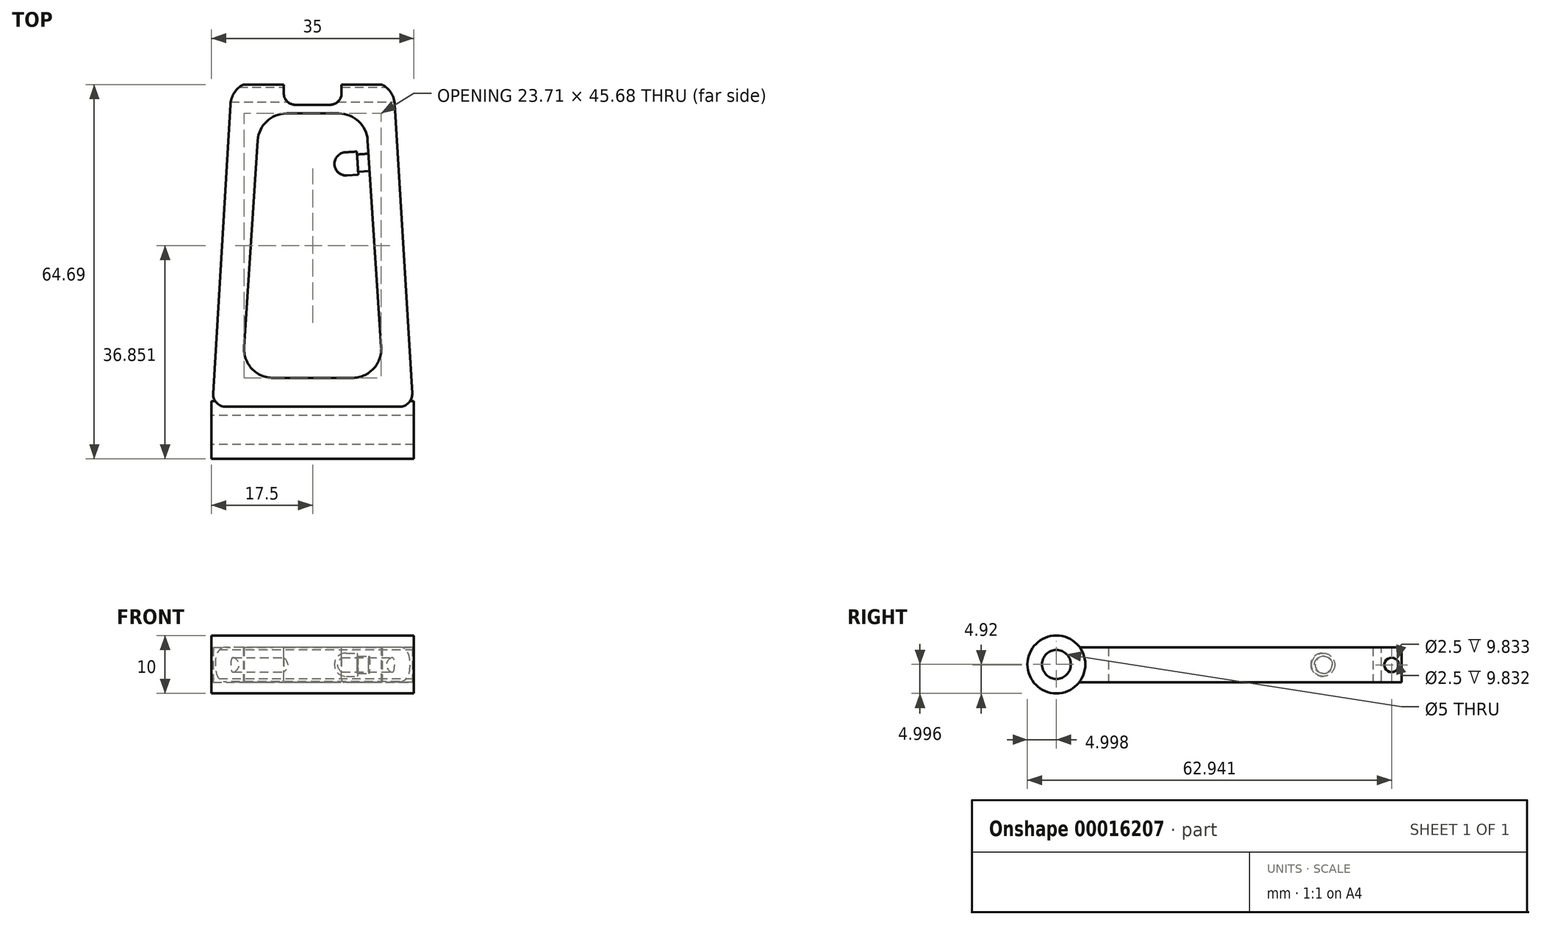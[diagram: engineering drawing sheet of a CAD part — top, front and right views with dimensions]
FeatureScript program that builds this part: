
annotation { "Feature Type Name" : "Feature", "Feature Type Description" : "" }
export const myFeature = defineFeature(function(context is Context, id is Id, definition is map)
    precondition{}
    {
        {
            var Q0;
            Q0=qCreatedBy(makeId("Top.planeOp"),FACE);
            var sketch = newSketch(context, id + "F0", { "sketchPlane" : qUnion([Q0])});
            skLineSegment(sketch, "E0", {"start": v(0, 0) * mm, "end": v(-15, 0) * mm});
            skArc(sketch, "E1", {"start": v(-15, 0) * mm, "mid": v(-16.6, 0.7) * mm, "end": v(-17.2, 2.34) * mm});
            skLineSegment(sketch, "E2", {"start": v(-17.2, 2.34) * mm, "end": v(-14.2, 52.25) * mm});
            skLineSegment(sketch, "E3", {"start": v(0, 28.16) * mm, "end": v(0, 0) * mm, "construction": true});
            skLineSegment(sketch, "E4.MirrorCS", {"start": v(17.2, 2.34) * mm, "end": v(14.2, 52.25) * mm});
            skArc(sketch, "E5.MirrorCS", {"start": v(15, 0) * mm, "mid": v(16.6, 0.7) * mm, "end": v(17.2, 2.34) * mm});
            skLineSegment(sketch, "E6.MirrorCS", {"start": v(0, 0) * mm, "end": v(15, 0) * mm});
            skArc(sketch, "E7", {"start": v(-14.2, 52.25) * mm, "mid": v(-13.55, 54.25) * mm, "end": v(-12, 55.68) * mm});
            skLineSegment(sketch, "E8", {"start": v(-12, 55.68) * mm, "end": v(0, 55.68) * mm});
            skLineSegment(sketch, "E9.MirrorCS", {"start": v(12, 55.68) * mm, "end": v(0, 55.68) * mm});
            skArc(sketch, "E10.MirrorCS", {"start": v(14.2, 52.25) * mm, "mid": v(13.55, 54.25) * mm, "end": v(12, 55.68) * mm});
            skLineSegment(sketch, "E11", {"start": v(-9.2, 50.68) * mm, "end": v(-12.2, 5) * mm});
            skLineSegment(sketch, "E12", {"start": v(-9.2, 50.68) * mm, "end": v(0, 50.68) * mm});
            skLineSegment(sketch, "E13", {"start": v(-12.2, 5) * mm, "end": v(0, 5) * mm});
            skLineSegment(sketch, "E14.MirrorCS", {"start": v(9.2, 50.68) * mm, "end": v(0, 50.68) * mm});
            skLineSegment(sketch, "E15.MirrorCS", {"start": v(9.2, 50.68) * mm, "end": v(12.2, 5) * mm});
            skLineSegment(sketch, "E16.MirrorCS", {"start": v(12.2, 5) * mm, "end": v(0, 5) * mm});
            skSolve(sketch);
        }
        {
            var Q0;
            Q0=makeQuery(id+"F0.imprint","IMPRINT",FACE,{"disambiguationData":[TD([[makeQuery(id+"F0.imprint","IMPRINT",EDGE,{"derivedFrom":sQuery(id+"F0.wireOp",EDGE,"E0")}),-1.0]])]});
            extrude(context, id + "F1", {"entities" : qUnion([Q0]), "depth" : 6 * mm});
        }
        {
            var Q0;
            Q0=makeQuery(id+"F1.opExtrude","SWEPT_EDGE",EDGE,{"disambiguationData":[OSD([sQuery(id+"F0.wireOp",EDGE,"E14.MirrorCS"),sQuery(id+"F0.wireOp",EDGE,"E15.MirrorCS")])]});
            var Q1;
            Q1=makeQuery(id+"F1.opExtrude","SWEPT_EDGE",EDGE,{"disambiguationData":[OSD([sQuery(id+"F0.wireOp",EDGE,"E15.MirrorCS"),sQuery(id+"F0.wireOp",EDGE,"E16.MirrorCS")])]});
            var Q2;
            Q2=makeQuery(id+"F1.opExtrude","SWEPT_EDGE",EDGE,{"disambiguationData":[OSD([sQuery(id+"F0.wireOp",EDGE,"E11"),sQuery(id+"F0.wireOp",EDGE,"E13")])]});
            var Q3;
            Q3=makeQuery(id+"F1.opExtrude","SWEPT_EDGE",EDGE,{"disambiguationData":[OSD([sQuery(id+"F0.wireOp",EDGE,"E11"),sQuery(id+"F0.wireOp",EDGE,"E12")])]});
            fillet(context, id + "F2", {"entities" : qUnion([Q0, Q1, Q2, Q3]), "radius" : 5 * mm, "tangentPropagation" : true, "allowEdgeOverflow" : false});
        }
        {
            var Q0;
            Q0=makeQuery(id+"F1.opExtrude","CAP_FACE",FACE,{"disambiguationData":[OSD([sQuery(id+"F0.wireOp",EDGE,"E0"),sQuery(id+"F0.wireOp",EDGE,"E1"),sQuery(id+"F0.wireOp",EDGE,"E2"),sQuery(id+"F0.wireOp",EDGE,"E4.MirrorCS"),sQuery(id+"F0.wireOp",EDGE,"E5.MirrorCS"),sQuery(id+"F0.wireOp",EDGE,"E6.MirrorCS"),sQuery(id+"F0.wireOp",EDGE,"E7"),sQuery(id+"F0.wireOp",EDGE,"E8"),sQuery(id+"F0.wireOp",EDGE,"E9.MirrorCS"),sQuery(id+"F0.wireOp",EDGE,"E10.MirrorCS"),sQuery(id+"F0.wireOp",EDGE,"E11"),sQuery(id+"F0.wireOp",EDGE,"E12"),sQuery(id+"F0.wireOp",EDGE,"E13"),sQuery(id+"F0.wireOp",EDGE,"E14.MirrorCS"),sQuery(id+"F0.wireOp",EDGE,"E15.MirrorCS"),sQuery(id+"F0.wireOp",EDGE,"E16.MirrorCS")])],"isStart":false});
            var sketch = newSketch(context, id + "F3", { "sketchPlane" : qUnion([Q0])});
            skLineSegment(sketch, "E17.rect.bottom", {"start": v(5, 55.68) * mm, "end": v(-5, 55.68) * mm});
            skLineSegment(sketch, "E17.rect.top", {"start": v(5, 52.18) * mm, "end": v(-5, 52.18) * mm});
            skLineSegment(sketch, "E17.rect.left", {"start": v(5, 55.68) * mm, "end": v(5, 52.18) * mm});
            skLineSegment(sketch, "E17.rect.right", {"start": v(-5, 55.68) * mm, "end": v(-5, 52.18) * mm});
            skPoint(sketch, "E17.rect.middle", {"position": v(0, 53.93) * mm});
            skSolve(sketch);
        }
        {
            var Q0;
            Q0=makeQuery(id+"F3.imprint","IMPRINT",FACE,{"disambiguationData":[TD([[makeQuery(id+"F3.imprint","IMPRINT",EDGE,{"derivedFrom":sQuery(id+"F3.wireOp",EDGE,"E17.rect.bottom")}),1.0]])]});
            extrude(context, id + "F4", {"entities" : qUnion([Q0]), "operationType" : NewBodyOperationType.REMOVE, "oppositeDirection" : true, "depth" : 25 * mm});
        }
        {
            var Q0;
            Q0=makeQuery(id+"F4.boolean.opBoolean","COPY",FACE,{"derivedFrom":makeQuery(id+"F4.opExtrude","SWEPT_FACE",FACE,{"disambiguationData":[OSD([sQuery(id+"F3.wireOp",EDGE,"E17.rect.right")])]})});
            var sketch = newSketch(context, id + "F5", { "sketchPlane" : qUnion([Q0])});
            skCircle(sketch, "E18", {"center": v(53.93, 3) * mm, "radius": 1.25 * mm});
            skSolve(sketch);
        }
        {
            var Q0;
            Q0=makeQuery(id+"F5.imprint","IMPRINT",FACE,{"disambiguationData":[TD([[makeQuery(id+"F5.imprint","IMPRINT",EDGE,{"derivedFrom":sQuery(id+"F5.wireOp",EDGE,"E18")}),1.0]])]});
            extrude(context, id + "F6", {"entities" : qUnion([Q0]), "operationType" : NewBodyOperationType.REMOVE, "endBound" : BoundingType.SYMMETRIC, "oppositeDirection" : true, "depth" : 40 * mm});
        }
        {
            var Q0;
            Q0=makeQuery(id+"F4.boolean.opBoolean","COPY",EDGE,{"derivedFrom":makeQuery(id+"F4.opExtrude","SWEPT_EDGE",EDGE,{"disambiguationData":[OSD([sQuery(id+"F3.wireOp",EDGE,"E17.rect.top"),sQuery(id+"F3.wireOp",EDGE,"E17.rect.right")])]})});
            var Q1;
            Q1=makeQuery(id+"F4.boolean.opBoolean","COPY",EDGE,{"derivedFrom":makeQuery(id+"F4.opExtrude","SWEPT_EDGE",EDGE,{"disambiguationData":[OSD([sQuery(id+"F3.wireOp",EDGE,"E17.rect.top"),sQuery(id+"F3.wireOp",EDGE,"E17.rect.left")])]})});
            fillet(context, id + "F7", {"entities" : qUnion([Q0, Q1]), "radius" : 2 * mm, "tangentPropagation" : true, "allowEdgeOverflow" : false});
        }
        {
            var Q0;
            Q0=makeQuery(id+"F4.boolean.opBoolean","COPY",EDGE,{"derivedFrom":makeQuery(id+"F4.opExtrude","CAP_EDGE",EDGE,{"disambiguationData":[OSD([sQuery(id+"F3.wireOp",EDGE,"E17.rect.top")])],"isStart":true})});
            var Q1;
            Q1=makeQuery(id+"F4.boolean.opBoolean","INTERSECT",EDGE,{"derivedFrom":[makeQuery(id+"F1.opExtrude","CAP_FACE",FACE,{"disambiguationData":[OSD([sQuery(id+"F0.wireOp",EDGE,"E0"),sQuery(id+"F0.wireOp",EDGE,"E1"),sQuery(id+"F0.wireOp",EDGE,"E2"),sQuery(id+"F0.wireOp",EDGE,"E4.MirrorCS"),sQuery(id+"F0.wireOp",EDGE,"E5.MirrorCS"),sQuery(id+"F0.wireOp",EDGE,"E6.MirrorCS"),sQuery(id+"F0.wireOp",EDGE,"E7"),sQuery(id+"F0.wireOp",EDGE,"E8"),sQuery(id+"F0.wireOp",EDGE,"E9.MirrorCS"),sQuery(id+"F0.wireOp",EDGE,"E10.MirrorCS"),sQuery(id+"F0.wireOp",EDGE,"E11"),sQuery(id+"F0.wireOp",EDGE,"E12"),sQuery(id+"F0.wireOp",EDGE,"E13"),sQuery(id+"F0.wireOp",EDGE,"E14.MirrorCS"),sQuery(id+"F0.wireOp",EDGE,"E15.MirrorCS"),sQuery(id+"F0.wireOp",EDGE,"E16.MirrorCS")])],"isStart":true}),makeQuery(id+"F4.opExtrude","SWEPT_FACE",FACE,{"disambiguationData":[OSD([sQuery(id+"F3.wireOp",EDGE,"E17.rect.top")])]})]});
            fillet(context, id + "F8", {"entities" : qUnion([Q0, Q1]), "radius" : .5 * mm, "tangentPropagation" : true, "allowEdgeOverflow" : false});
        }
        {
            var Q0;
            Q0=qCreatedBy(makeId("Right.planeOp"),FACE);
            var sketch = newSketch(context, id + "F9", { "sketchPlane" : qUnion([Q0])});
            skCircle(sketch, "E19", {"center": v(-4.01, 3.08) * mm, "radius": 5 * mm});
            skSolve(sketch);
        }
        {
            var Q0;
            Q0=makeQuery(id+"F9.imprint","IMPRINT",FACE,{"disambiguationData":[TD([[makeQuery(id+"F9.imprint","IMPRINT",EDGE,{"derivedFrom":sQuery(id+"F9.wireOp",EDGE,"E19")}),1.0]])]});
            extrude(context, id + "F10", {"entities" : qUnion([Q0]), "operationType" : NewBodyOperationType.ADD, "endBound" : BoundingType.SYMMETRIC, "depth" : 35 * mm});
        }
        {
            var Q0;
            Q0=makeQuery(id+"F10.opExtrude","CAP_FACE",FACE,{"disambiguationData":[OSD([sQuery(id+"F9.wireOp",EDGE,"E19")])],"isStart":true});
            var sketch = newSketch(context, id + "F11", { "sketchPlane" : qUnion([Q0])});
            skCircle(sketch, "E20", {"center": v(4.01, 3.08) * mm, "radius": 2.5 * mm});
            skSolve(sketch);
        }
        {
            var Q0;
            Q0=makeQuery(id+"F11.imprint","IMPRINT",FACE,{"disambiguationData":[TD([[makeQuery(id+"F11.imprint","IMPRINT",EDGE,{"derivedFrom":sQuery(id+"F11.wireOp",EDGE,"E20")}),1.0]])]});
            extrude(context, id + "F12", {"entities" : qUnion([Q0]), "operationType" : NewBodyOperationType.REMOVE, "oppositeDirection" : true, "depth" : 35 * mm});
        }
        {
            var Q0;
            Q0=makeQuery(id+"F1.opExtrude","SWEPT_FACE",FACE,{"disambiguationData":[OSD([sQuery(id+"F0.wireOp",EDGE,"E15.MirrorCS")])]});
            var sketch = newSketch(context, id + "F13", { "sketchPlane" : qUnion([Q0])});
            skCircle(sketch, "E21", {"center": v(-41.5, 3.02) * mm, "radius": 1.5 * mm});
            skSolve(sketch);
        }
        {
            var Q0;
            Q0=makeQuery(id+"F13.imprint","IMPRINT",FACE,{"disambiguationData":[TD([[makeQuery(id+"F13.imprint","IMPRINT",EDGE,{"derivedFrom":sQuery(id+"F13.wireOp",EDGE,"E21")}),1.0]])]});
            extrude(context, id + "F14", {"entities" : qUnion([Q0]), "operationType" : NewBodyOperationType.ADD, "depth" : 2 * mm});
        }
        {
            var Q0;
            Q0=makeQuery(id+"F14.opExtrude","CAP_FACE",FACE,{"disambiguationData":[OSD([sQuery(id+"F13.wireOp",EDGE,"E21")])],"isStart":false});
            var sketch = newSketch(context, id + "F15", { "sketchPlane" : qUnion([Q0])});
            skCircle(sketch, "E22", {"center": v(-41.5, 3.02) * mm, "radius": 2 * mm});
            skSolve(sketch);
        }
        {
            var Q0;
            Q0=makeQuery(id+"F15.imprint","IMPRINT",FACE,{"disambiguationData":[TD([[makeQuery(id+"F15.imprint","IMPRINT",EDGE,{"derivedFrom":makeQuery(id+"F14.opExtrude","CAP_EDGE",EDGE,{"disambiguationData":[OSD([sQuery(id+"F13.wireOp",EDGE,"E21")])],"isStart":false})}),1.0]])]});
            var Q1;
            Q1=makeQuery(id+"F15.imprint","IMPRINT",FACE,{"disambiguationData":[TD([[makeQuery(id+"F15.imprint","IMPRINT",EDGE,{"derivedFrom":sQuery(id+"F15.wireOp",EDGE,"E22")}),1.0]])]});
            extrude(context, id + "F16", {"entities" : qUnion([Q0, Q1]), "operationType" : NewBodyOperationType.ADD, "depth" : 4 * mm});
        }
        {
            var Q0;
            Q0=makeQuery(id+"F16.opExtrude","CAP_EDGE",EDGE,{"disambiguationData":[OSD([sQuery(id+"F15.wireOp",EDGE,"E22")])],"isStart":false});
            fillet(context, id + "F17", {"entities" : qUnion([Q0]), "radius" : 2 * mm, "tangentPropagation" : true, "allowEdgeOverflow" : false});
        }
    });
